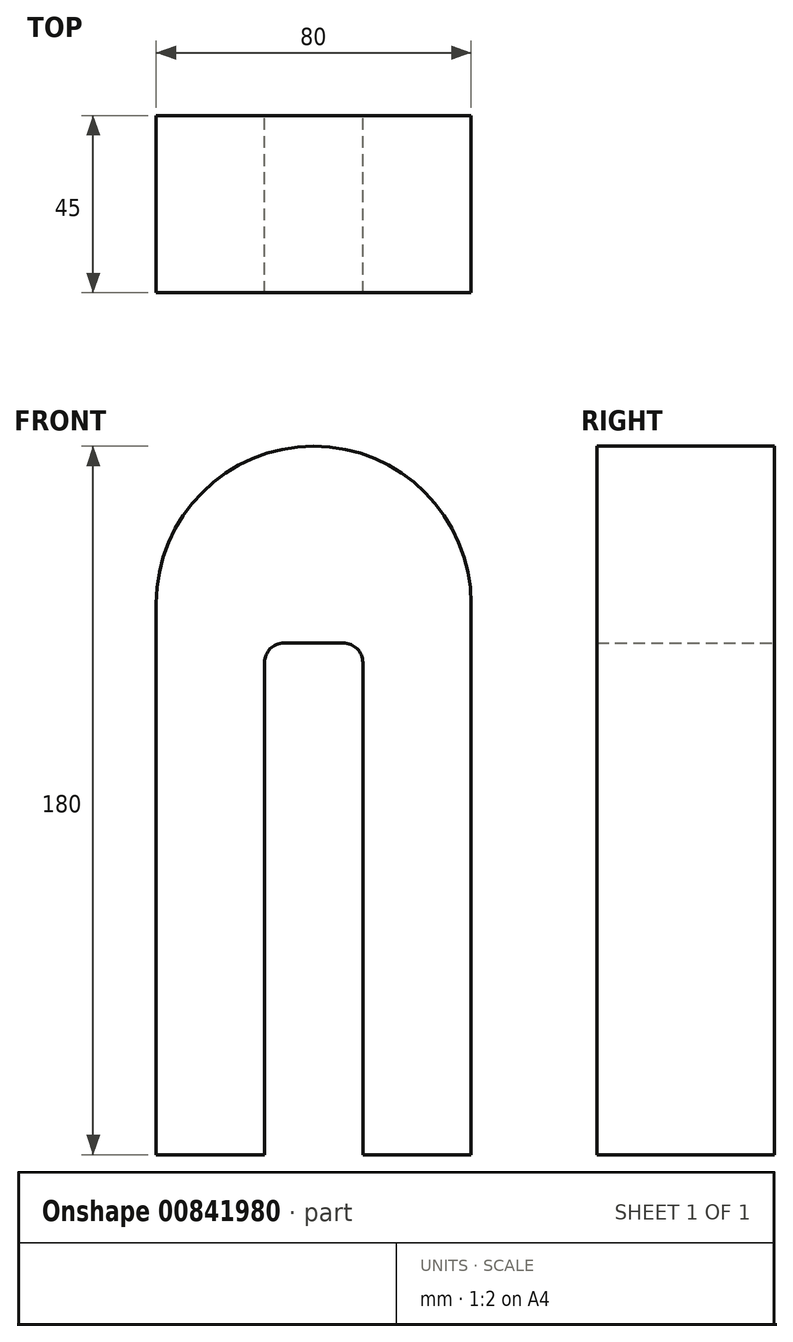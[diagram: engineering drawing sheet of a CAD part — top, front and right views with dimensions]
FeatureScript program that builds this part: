
annotation { "Feature Type Name" : "Feature", "Feature Type Description" : "" }
export const myFeature = defineFeature(function(context is Context, id is Id, definition is map)
    precondition{}
    {
        {
            var Q0;
            Q0=qCreatedBy(makeId("Front.planeOp"),FACE);
            var sketch = newSketch(context, id + "F0", { "sketchPlane" : qUnion([Q0])});
            skLineSegment(sketch, "E0.bottom", {"start": v(40, -90) * mm, "end": v(-40, -90) * mm});
            skLineSegment(sketch, "E0.top", {"start": v(40, 90) * mm, "end": v(-40, 90) * mm});
            skLineSegment(sketch, "E0.left", {"start": v(40, -90) * mm, "end": v(40, 90) * mm});
            skLineSegment(sketch, "E0.right", {"start": v(-40, -90) * mm, "end": v(-40, 90) * mm});
            skPoint(sketch, "E0.middle", {"position": v(0, 0) * mm});
            skLineSegment(sketch, "E1", {"start": v(-40, -90) * mm, "end": v(-12.5, -90) * mm});
            skLineSegment(sketch, "E2", {"start": v(40, -90) * mm, "end": v(12.5, -90) * mm});
            skLineSegment(sketch, "E3", {"start": v(12.5, -90) * mm, "end": v(-12.5, -90) * mm});
            skLineSegment(sketch, "E4", {"start": v(-40, 90) * mm, "end": v(-40, 50) * mm});
            skArc(sketch, "E5", {"start": v(0, 90) * mm, "mid": v(-28.28, 78.28) * mm, "end": v(-40, 50) * mm});
            skArc(sketch, "E6", {"start": v(40, 50) * mm, "mid": v(28.28, 78.28) * mm, "end": v(0, 90) * mm});
            skLineSegment(sketch, "E7", {"start": v(-12.5, -90) * mm, "end": v(-12.5, 35) * mm});
            skLineSegment(sketch, "E8", {"start": v(12.5, -90) * mm, "end": v(12.5, 35) * mm});
            skLineSegment(sketch, "E9", {"start": v(7.5, 40) * mm, "end": v(-7.5, 40) * mm});
            skPoint(sketch, "E10.visualSharp", {"position": v(-12.5, 40) * mm});
            skArc(sketch, "E10.filletArc", {"start": v(-7.5, 40) * mm, "mid": v(-11.04, 38.54) * mm, "end": v(-12.5, 35) * mm});
            skPoint(sketch, "E11.visualSharp", {"position": v(12.5, 40) * mm});
            skArc(sketch, "E11.filletArc", {"start": v(12.5, 35) * mm, "mid": v(11.04, 38.54) * mm, "end": v(7.5, 40) * mm});
            skSolve(sketch);
        }
        {
            var Q0;
            {var subQ1=sQuery(id+"F0.wireOp",EDGE,"E5");Q0=makeQuery(id+"F0.imprint","IMPRINT",FACE,{"disambiguationData":[TD([[makeQuery(id+"F0.imprint","IMPRINT",EDGE,{"derivedFrom":subQ1}),1.0]])]});}
            extrude(context, id + "F1", {"entities" : qUnion([Q0]), "depth" : 45 * mm, "offsetDistance" : 25 * mm});
        }
    });
